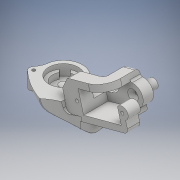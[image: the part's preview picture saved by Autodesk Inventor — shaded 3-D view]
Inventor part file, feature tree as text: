
AUTODESK INVENTOR PART (.ipt)
format: ipt  version: 2018 (Build 220112000, 112)  size: 1,013,760 bytes
history: native  units: mm
features: other x24, extrude x8, sketch x8, projected_geometry x5, reference x2, chamfer x1
ambient origin geometry x8: Origin, YZ Plane, XZ Plane, XY Plane, X Axis, Y Axis, Z Axis, Center Point
bodies: Body1 (feature_tree)
feature tree (48):
  other  "ソリッド1"
  other  "ダイレクト編集1"
  extrude  "押し出し1"  Depth=8.8365mm
  extrude  "押し出し2"  Depth=0.3mm
  extrude  "押し出し3"  Depth=5.0mm
  extrude  "押し出し4"  Depth=12.5mm TaperAngle=0.0deg
  extrude  "押し出し5"  Depth=10.0mm TaperAngle=0.0deg
  extrude  "押し出し6"  Depth=10.0mm TaperAngle=0.0deg
  extrude  "押し出し7"  Depth=10.0mm TaperAngle=0.0deg
  other  "ダイレクト編集2"
  chamfer  "面取り1"  Distance=10.0mm
  other  "ダイレクト編集3"
  other  "ダイレクト編集4"
  other  "ダイレクト編集5"
  extrude  "押し出し9"  Depth=10.0mm TaperAngle=0.0deg
  other  "ダイレクト編集6"
  other  "ダイレクト編集7"
  sketch  "スケッチ1"
  reference  "参照1"
  reference  "参照2"
  sketch  "スケッチ2"
  projected_geometry  "投影ループ1"
  sketch  "スケッチ3"
  projected_geometry  "投影ループ2"
  sketch  "スケッチ4"
  sketch  "スケッチ5"
  projected_geometry  "投影ループ3"
  sketch  "スケッチ6"
  projected_geometry  "投影ループ4"
  projected_geometry  "投影ループ5"
  sketch  "スケッチ7"
  sketch  "スケッチ9"
  other  "尺度1"
  parser-record x1  (decoder bookkeeping rows leaked as tree rows — omitted from the tree; the rows remain in map.json)
  other  "M-R-T.iam"
  other  "Servo_HK282A:1"
  other  "削除1"
  other  "削除2"
  other  "移動1"
  other  "サイズ1"
  other  "サイズ2"
  other  "サイズ3"
  other  "サイズ4"
  other  "サイズ5"
  other  "サイズ6"
  other  "サイズ7"
  other  "サイズ8"
  other  "サイズ9"
note: 1 file-system path scrubbed to <path> (originals preserved in map.json)
